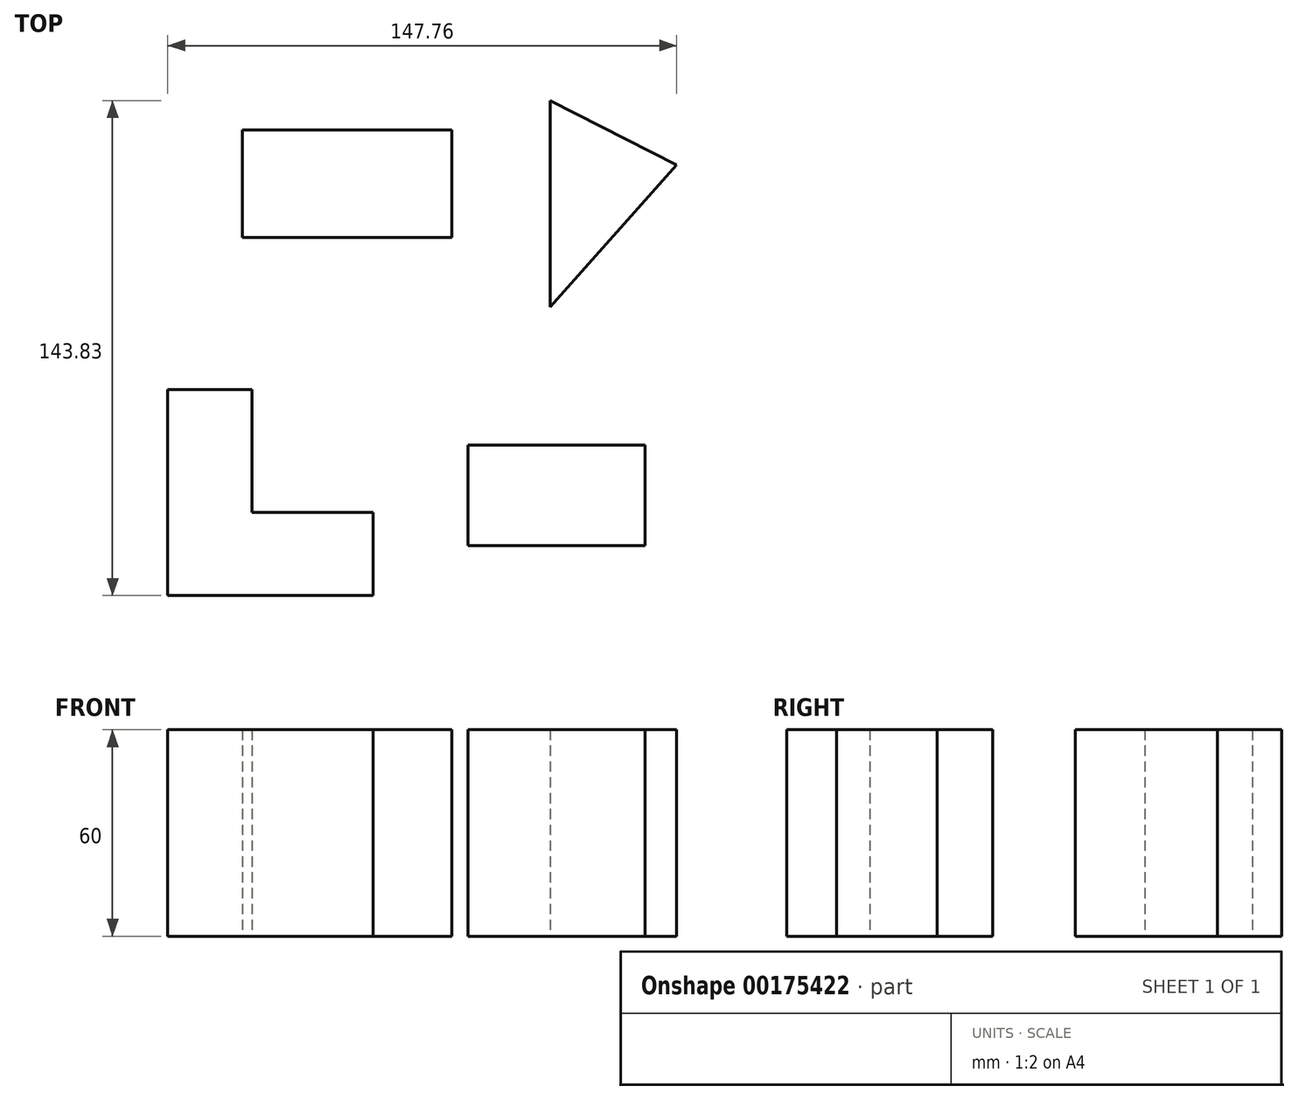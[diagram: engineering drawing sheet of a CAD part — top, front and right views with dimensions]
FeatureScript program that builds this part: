
annotation { "Feature Type Name" : "Feature", "Feature Type Description" : "" }
export const myFeature = defineFeature(function(context is Context, id is Id, definition is map)
    precondition{}
    {
        {
            var Q0;
            Q0=qCreatedBy(makeId("Top.planeOp"),FACE);
            var sketch = newSketch(context, id + "F0", { "sketchPlane" : qUnion([Q0])});
            skLineSegment(sketch, "E0.bottom", {"start": v(-53.6, 60.63) * mm, "end": v(7.33, 60.63) * mm});
            skLineSegment(sketch, "E0.top", {"start": v(-53.6, 29.4) * mm, "end": v(7.33, 29.4) * mm});
            skLineSegment(sketch, "E0.left", {"start": v(-53.6, 60.63) * mm, "end": v(-53.6, 29.4) * mm});
            skLineSegment(sketch, "E0.right", {"start": v(7.33, 60.63) * mm, "end": v(7.33, 29.4) * mm});
            skSolve(sketch);
        }
        {
            var Q0;
            Q0=makeQuery(id+"F0.imprint","IMPRINT",FACE,{"disambiguationData":[TD([[makeQuery(id+"F0.imprint","IMPRINT",EDGE,{"derivedFrom":sQuery(id+"F0.wireOp",EDGE,"E0.bottom")}),-1.0]])]});
            var sketch = newSketch(context, id + "F1", { "sketchPlane" : qUnion([Q0])});
            skLineSegment(sketch, "E1.bottom", {"start": v(35.8, 69.16) * mm, "end": v(72.56, 50.42) * mm});
            skLineSegment(sketch, "E1.left", {"start": v(35.8, 69.16) * mm, "end": v(35.8, 9.16) * mm});
            skLineSegment(sketch, "E2", {"start": v(72.56, 50.42) * mm, "end": v(35.8, 9.16) * mm});
            skSolve(sketch);
        }
        {
            var Q0;
            Q0=qCreatedBy(makeId("Top.planeOp"),FACE);
            var sketch = newSketch(context, id + "F2", { "sketchPlane" : qUnion([Q0])});
            skLineSegment(sketch, "E3.bottom", {"start": v(-75.2, -74.67) * mm, "end": v(-15.56, -74.67) * mm});
            skLineSegment(sketch, "E3.top", {"start": v(-75.2, -14.83) * mm, "end": v(-50.7, -14.83) * mm});
            skLineSegment(sketch, "E3.left", {"start": v(-75.2, -74.67) * mm, "end": v(-75.2, -14.83) * mm});
            skLineSegment(sketch, "E3.right", {"start": v(-15.56, -74.67) * mm, "end": v(-15.56, -50.57) * mm});
            skLineSegment(sketch, "E4.top", {"start": v(-50.7, -50.57) * mm, "end": v(-15.56, -50.57) * mm});
            skLineSegment(sketch, "E4.left", {"start": v(-50.7, -14.83) * mm, "end": v(-50.7, -50.57) * mm});
            skSolve(sketch);
        }
        {
            var Q0;
            Q0=makeQuery(id+"F1.imprint","IMPRINT",FACE,{"disambiguationData":[TD([[makeQuery(id+"F1.imprint","IMPRINT",EDGE,{"derivedFrom":sQuery(id+"F1.wireOp",EDGE,"E1.bottom")}),-1.0]])]});
            extrude(context, id + "F3", {"entities" : qUnion([Q0]), "depth" : 60 * mm});
        }
        {
            var Q0;
            Q0=makeQuery(id+"F2.imprint","IMPRINT",FACE,{"disambiguationData":[TD([[makeQuery(id+"F2.imprint","IMPRINT",EDGE,{"derivedFrom":sQuery(id+"F2.wireOp",EDGE,"E3.bottom")}),1.0]])]});
            extrude(context, id + "F4", {"entities" : qUnion([Q0]), "depth" : 60 * mm});
        }
        {
            var Q0;
            Q0=makeQuery(id+"F0.imprint","IMPRINT",FACE,{"disambiguationData":[TD([[makeQuery(id+"F0.imprint","IMPRINT",EDGE,{"derivedFrom":sQuery(id+"F0.wireOp",EDGE,"E0.bottom")}),-1.0]])]});
            extrude(context, id + "F5", {"entities" : qUnion([Q0]), "depth" : 60 * mm});
        }
        {
            var Q0;
            Q0=qCreatedBy(makeId("Top.planeOp"),FACE);
            var sketch = newSketch(context, id + "F6", { "sketchPlane" : qUnion([Q0])});
            skLineSegment(sketch, "E5.bottom", {"start": v(11.95, -30.94) * mm, "end": v(63.42, -30.94) * mm});
            skLineSegment(sketch, "E5.top", {"start": v(11.95, -60.24) * mm, "end": v(63.42, -60.24) * mm});
            skLineSegment(sketch, "E5.left", {"start": v(11.95, -30.94) * mm, "end": v(11.95, -60.24) * mm});
            skLineSegment(sketch, "E5.right", {"start": v(63.42, -30.94) * mm, "end": v(63.42, -60.24) * mm});
            skSolve(sketch);
        }
        {
            var Q0;
            Q0=makeQuery(id+"F6.imprint","IMPRINT",FACE,{"disambiguationData":[TD([[makeQuery(id+"F6.imprint","IMPRINT",EDGE,{"derivedFrom":sQuery(id+"F6.wireOp",EDGE,"E5.bottom")}),-1.0]])]});
            extrude(context, id + "F7", {"entities" : qUnion([Q0]), "depth" : 60 * mm});
        }
    });
